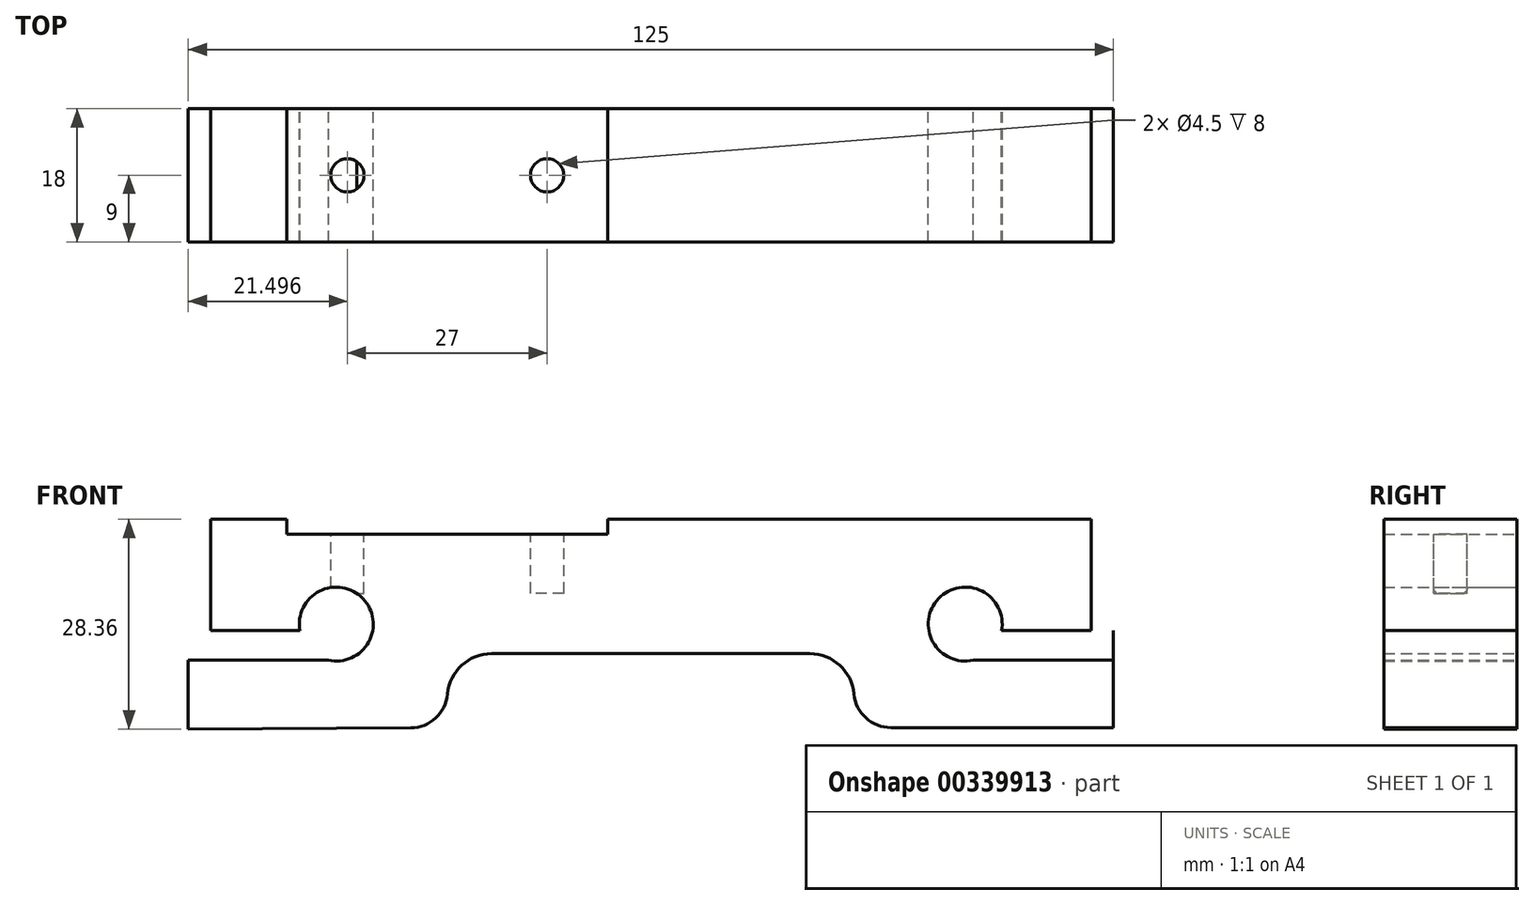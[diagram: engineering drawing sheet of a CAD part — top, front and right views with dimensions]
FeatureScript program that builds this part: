
annotation { "Feature Type Name" : "Feature", "Feature Type Description" : "" }
export const myFeature = defineFeature(function(context is Context, id is Id, definition is map)
    precondition{}
    {
        {
            var Q0;
            Q0=qCreatedBy(makeId("Front.planeOp"),FACE);
            var sketch = newSketch(context, id + "F0", { "sketchPlane" : qUnion([Q0])});
            skCircle(sketch, "E0", {"center": v(-59.3, 26.15) * mm, "radius": 5 * mm});
            skCircle(sketch, "E1", {"center": v(25.7, 26.15) * mm, "radius": 5 * mm});
            skLineSegment(sketch, "E2", {"start": v(-59.3, 26.15) * mm, "end": v(25.7, 26.15) * mm, "construction": true});
            skLineSegment(sketch, "E3.right", {"start": v(45.7, 25.27) * mm, "end": v(45.7, 12.15) * mm});
            skLineSegment(sketch, "E4", {"start": v(-79.3, 26.15) * mm, "end": v(-59.3, 26.15) * mm, "construction": true});
            skLineSegment(sketch, "E5", {"start": v(25.7, 26.15) * mm, "end": v(45.7, 26.15) * mm, "construction": true});
            skLineSegment(sketch, "E6", {"start": v(16.07, 26.15) * mm, "end": v(16.07, 40.15) * mm, "construction": true});
            skLineSegment(sketch, "E7.bottom", {"start": v(-79.3, 25.27) * mm, "end": v(-59.37, 25.27) * mm});
            skLineSegment(sketch, "E7.top", {"start": v(-79.3, 21.27) * mm, "end": v(-59.37, 21.27) * mm});
            skLineSegment(sketch, "E7.right", {"start": v(-59.37, 25.27) * mm, "end": v(-59.37, 21.27) * mm});
            skLineSegment(sketch, "E8.bottom", {"start": v(45.7, 25.27) * mm, "end": v(25.95, 25.27) * mm});
            skLineSegment(sketch, "E8.top", {"start": v(45.7, 21.27) * mm, "end": v(25.95, 21.27) * mm});
            skLineSegment(sketch, "E8.left", {"start": v(45.7, 25.27) * mm, "end": v(45.7, 21.27) * mm});
            skLineSegment(sketch, "E8.right", {"start": v(25.95, 25.27) * mm, "end": v(25.95, 21.27) * mm});
            skLineSegment(sketch, "E9", {"start": v(16.07, 26.15) * mm, "end": v(16.07, 12.15) * mm, "construction": true});
            skLineSegment(sketch, "E10", {"start": v(-38.3, 22.15) * mm, "end": v(4.7, 22.15) * mm});
            skLineSegment(sketch, "E11", {"start": v(-44.3, 16.15) * mm, "end": v(-44.3, 12.15) * mm});
            skLineSegment(sketch, "E12", {"start": v(10.7, 16.15) * mm, "end": v(10.7, 12.15) * mm});
            skPoint(sketch, "E13.visualSharp", {"position": v(10.7, 22.15) * mm});
            skArc(sketch, "E13.filletArc", {"start": v(10.7, 16.15) * mm, "mid": v(8.94, 20.4) * mm, "end": v(4.7, 22.15) * mm});
            skPoint(sketch, "E14.visualSharp", {"position": v(-44.3, 22.15) * mm});
            skArc(sketch, "E14.filletArc", {"start": v(-38.3, 22.15) * mm, "mid": v(-42.55, 20.4) * mm, "end": v(-44.3, 16.15) * mm});
            skLineSegment(sketch, "E15", {"start": v(9.56, 40.32) * mm, "end": v(34.4, 40.32) * mm});
            skPoint(sketch, "E16.visualSharp", {"position": v(-79.22, 58.15) * mm});
            skLineSegment(sketch, "E17", {"start": v(-79.3, 11.96) * mm, "end": v(-44.3, 12.15) * mm});
            skLineSegment(sketch, "E18", {"start": v(10.7, 12.15) * mm, "end": v(45.7, 12.15) * mm});
            skLineSegment(sketch, "E19", {"start": v(9.56, 40.32) * mm, "end": v(-80.57, 40.32) * mm});
            skLineSegment(sketch, "E20", {"start": v(-44.3, 12.15) * mm, "end": v(-44.3, 40.32) * mm, "construction": true});
            skLineSegment(sketch, "E21.bottom", {"start": v(-44.3, 40.32) * mm, "end": v(-22.6, 40.32) * mm});
            skLineSegment(sketch, "E21.top", {"start": v(-44.3, 38.32) * mm, "end": v(-22.6, 38.32) * mm});
            skLineSegment(sketch, "E21.left", {"start": v(-44.3, 40.32) * mm, "end": v(-44.3, 38.32) * mm});
            skLineSegment(sketch, "E21.right", {"start": v(-22.6, 40.32) * mm, "end": v(-22.6, 38.32) * mm});
            skLineSegment(sketch, "E22.bottom", {"start": v(-44.3, 38.32) * mm, "end": v(-66, 38.32) * mm});
            skLineSegment(sketch, "E22.top", {"start": v(-44.3, 40.32) * mm, "end": v(-66, 40.32) * mm});
            skLineSegment(sketch, "E22.left", {"start": v(-44.3, 38.32) * mm, "end": v(-44.3, 40.32) * mm});
            skLineSegment(sketch, "E22.right", {"start": v(-66, 38.32) * mm, "end": v(-66, 40.32) * mm});
            skLineSegment(sketch, "E23", {"start": v(-79.3, 11.96) * mm, "end": v(-79.3, 25.27) * mm});
            skLineSegment(sketch, "E24", {"start": v(-76.3, 25.27) * mm, "end": v(-76.3, 40.32) * mm});
            skLineSegment(sketch, "E25", {"start": v(42.7, 25.22) * mm, "end": v(42.7, 40.32) * mm});
            skLineSegment(sketch, "E26", {"start": v(42.7, 40.32) * mm, "end": v(34.4, 40.32) * mm});
            skLineSegment(sketch, "E27", {"start": v(42.7, 21.27) * mm, "end": v(42.7, 25.22) * mm});
            skSolve(sketch);
        }
        {
            var Q0;
            {var subQ15=sQuery(id+"F0.wireOp",EDGE,"E3.right");Q0=makeQuery(id+"F0.imprint","IMPRINT",FACE,{"disambiguationData":[TD([[makeQuery(id+"F0.imprint","IMPRINT",EDGE,{"derivedFrom":subQ15}),-1.0]])]});}
            extrude(context, id + "F1", {"entities" : qUnion([Q0]), "depth" : 18 * mm});
        }
        {
            var Q0;
            Q0=makeQuery(id+"F1.opExtrude","SWEPT_EDGE",EDGE,{"disambiguationData":[OSD([sQuery(id+"F0.wireOp",EDGE,"0bs0GA9L-5yHt-FVK7-Cz8Z-SRDizBf9nc71"),sQuery(id+"F0.wireOp",EDGE,"YlEYWXjf-oBkf-SdcC-s5Ip-Q7bDtR7lr0Xb")])]});
            var Q1;
            Q1=makeQuery(id+"F1.opExtrude","SWEPT_EDGE",EDGE,{"disambiguationData":[OSD([sQuery(id+"F0.wireOp",EDGE,"E1SxCpXs-l7QO-96rg-8xLE-IlAGUL5N2YJL"),sQuery(id+"F0.wireOp",EDGE,"8EBUzVXK-Ggkd-mSwv-9IIB-3syLRvhQxpJt")])]});
            var Q2;
            Q2=makeQuery(id+"F1.opExtrude","SWEPT_EDGE",EDGE,{"disambiguationData":[OSD([sQuery(id+"F0.wireOp",EDGE,"E11"),sQuery(id+"F0.wireOp",EDGE,"E17")])]});
            var Q3;
            Q3=makeQuery(id+"F1.opExtrude","SWEPT_EDGE",EDGE,{"disambiguationData":[OSD([sQuery(id+"F0.wireOp",EDGE,"E12"),sQuery(id+"F0.wireOp",EDGE,"E18")])]});
            fillet(context, id + "F2", {"entities" : qUnion([Q0, Q1, Q2, Q3]), "radius" : 5 * mm, "tangentPropagation" : true, "allowEdgeOverflow" : false});
        }
        {
            var Q0;
            Q0=makeQuery(id+"F1.opExtrude","SWEPT_FACE",FACE,{"disambiguationData":[OSD([sQuery(id+"F0.wireOp",EDGE,"E21.top"),sQuery(id+"F0.wireOp",EDGE,"E22.bottom")])]});
            var sketch = newSketch(context, id + "F3", { "sketchPlane" : qUnion([Q0])});
            skLineSegment(sketch, "E28", {"start": v(-66, -9) * mm, "end": v(-22.6, -9) * mm, "construction": true});
            skLineSegment(sketch, "E29", {"start": v(-44.3, 0) * mm, "end": v(-44.3, -18) * mm, "construction": true});
            skCircle(sketch, "E30", {"center": v(-57.8, -9) * mm, "radius": 2.25 * mm});
            skCircle(sketch, "E31", {"center": v(-30.8, -9) * mm, "radius": 2.25 * mm});
            skSolve(sketch);
        }
        {
            var Q0;
            Q0=makeQuery(id+"F3.imprint","IMPRINT",FACE,{"disambiguationData":[TD([[makeQuery(id+"F3.imprint","IMPRINT",EDGE,{"derivedFrom":sQuery(id+"F3.wireOp",EDGE,"E31")}),1.0]])]});
            var Q1;
            Q1=makeQuery(id+"F3.imprint","IMPRINT",FACE,{"disambiguationData":[TD([[makeQuery(id+"F3.imprint","IMPRINT",EDGE,{"derivedFrom":sQuery(id+"F3.wireOp",EDGE,"E30")}),1.0]])]});
            var Q2;
            Q2=sQuery(id+"F3.wireOp",EDGE,"E30");
            var Q3;
            Q3=sQuery(id+"F3.wireOp",EDGE,"E31");
            extrude(context, id + "F4", {"entities" : qUnion([Q0, Q1]), "operationType" : NewBodyOperationType.REMOVE, "surfaceEntities" : qUnion([Q2, Q3]), "oppositeDirection" : true, "depth" : 8 * mm});
        }
    });
